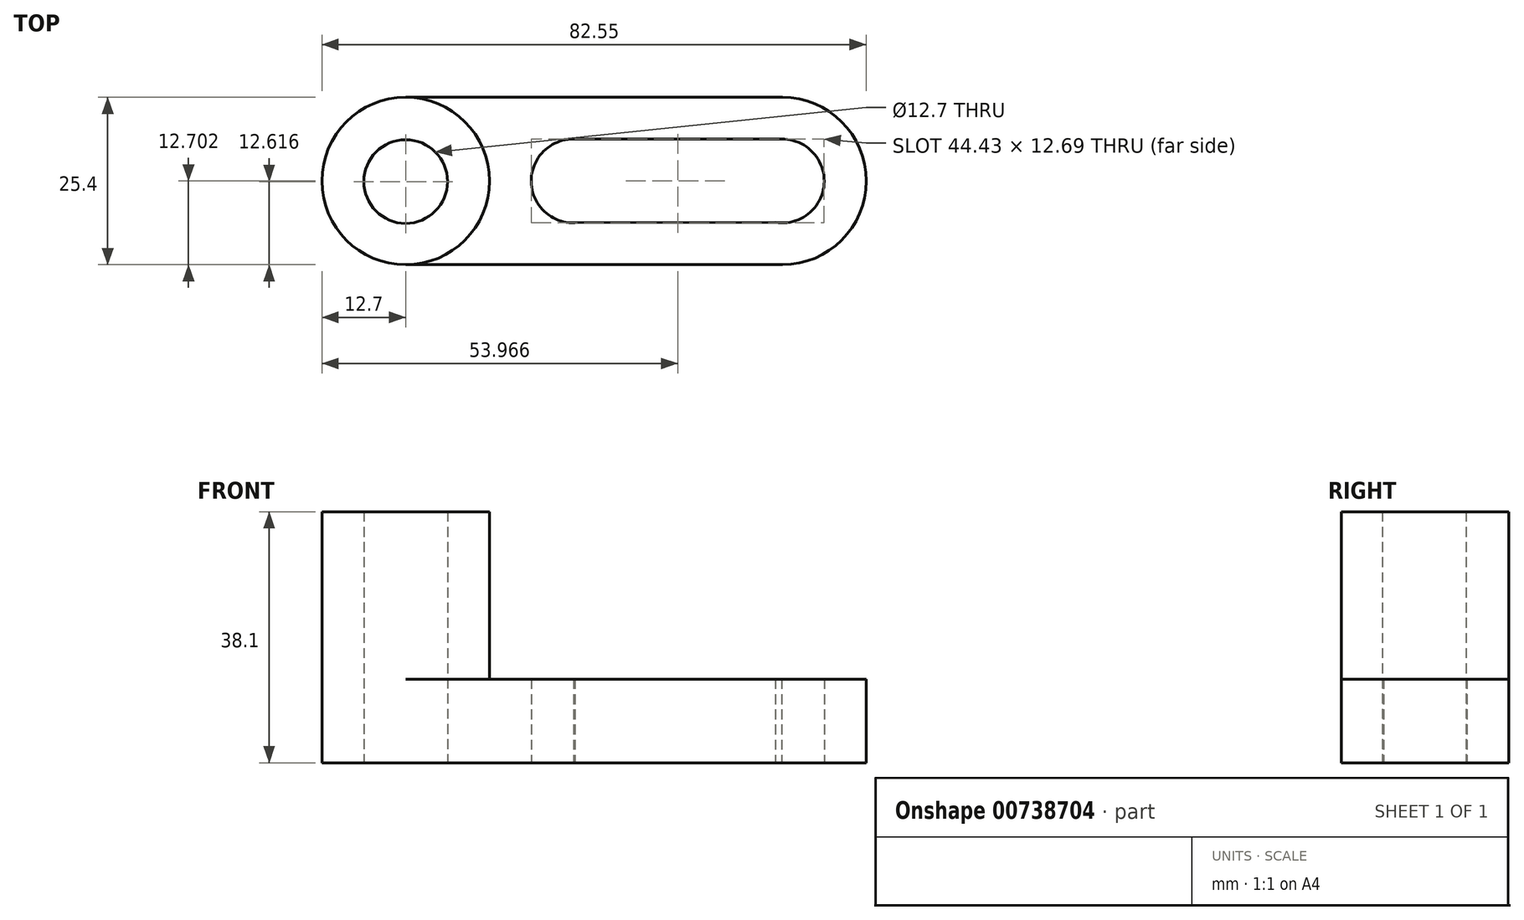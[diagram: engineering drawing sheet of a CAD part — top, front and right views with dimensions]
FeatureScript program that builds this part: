
annotation { "Feature Type Name" : "Feature", "Feature Type Description" : "" }
export const myFeature = defineFeature(function(context is Context, id is Id, definition is map)
    precondition{}
    {
        {
            var Q0;
            Q0=qCreatedBy(makeId("Front.planeOp"),FACE);
            var sketch = newSketch(context, id + "F0", { "sketchPlane" : qUnion([Q0])});
            skLineSegment(sketch, "E0", {"start": v(0, 38.1) * mm, "end": v(0, 0) * mm});
            skLineSegment(sketch, "E1", {"start": v(0, 0) * mm, "end": v(82.55, 0) * mm});
            skLineSegment(sketch, "E2", {"start": v(82.55, 0) * mm, "end": v(82.55, 12.7) * mm});
            skLineSegment(sketch, "E3", {"start": v(82.55, 12.7) * mm, "end": v(25.4, 12.7) * mm});
            skLineSegment(sketch, "E4", {"start": v(25.4, 12.7) * mm, "end": v(25.4, 38.1) * mm});
            skLineSegment(sketch, "E5", {"start": v(25.4, 38.1) * mm, "end": v(0, 38.1) * mm});
            skSolve(sketch);
        }
        {
            var Q0;
            Q0 = qSketchRegion(id + "F0", true);
            extrude(context, id + "F1", {"entities" : qUnion([Q0]), "depth" : 25.4 * mm, "offsetDistance" : 25.4 * mm});
        }
        {
            var Q0;
            Q0=qCreatedBy(makeId("Top.planeOp"),FACE);
            var sketch = newSketch(context, id + "F2", { "sketchPlane" : qUnion([Q0])});
            skCircle(sketch, "E6", {"center": v(12.7, -12.7) * mm, "radius": 12.7 * mm});
            skLineSegment(sketch, "E7", {"start": v(25.4, 0) * mm, "end": v(25.4, -25.4) * mm});
            skLineSegment(sketch, "E8", {"start": v(25.4, -25.4) * mm, "end": v(0, -25.4) * mm});
            skLineSegment(sketch, "E9", {"start": v(0, -25.4) * mm, "end": v(0, 0) * mm});
            skLineSegment(sketch, "E10", {"start": v(0, 0) * mm, "end": v(25.4, 0) * mm});
            skSolve(sketch);
        }
        {
            var Q0;
            Q0=qCreatedBy(makeId("Front.planeOp"),FACE);
            var sketch = newSketch(context, id + "F3", { "sketchPlane" : qUnion([Q0])});
            skLineSegment(sketch, "E11", {"start": v(25.4, 12.7) * mm, "end": v(0, 12.7) * mm});
            skLineSegment(sketch, "E12", {"start": v(0, 12.7) * mm, "end": v(0, 38.1) * mm});
            skLineSegment(sketch, "E13", {"start": v(0, 38.1) * mm, "end": v(25.4, 38.1) * mm});
            skLineSegment(sketch, "E14", {"start": v(25.4, 38.1) * mm, "end": v(25.4, 12.7) * mm});
            skSolve(sketch);
        }
        {
            var Q0;
            Q0 = qSketchRegion(id + "F3", true);
            extrude(context, id + "F4", {"entities" : qUnion([Q0]), "operationType" : NewBodyOperationType.REMOVE, "endBound" : BoundingType.THROUGH_ALL, "depth" : 25.4 * mm, "offsetDistance" : 25.4 * mm});
        }
        {
            var Q0;
            Q0=qCreatedBy(makeId("Top.planeOp"),FACE);
            var sketch = newSketch(context, id + "F5", { "sketchPlane" : qUnion([Q0])});
            skCircle(sketch, "E15", {"center": v(12.7, -12.7) * mm, "radius": 12.7 * mm});
            skSolve(sketch);
        }
        {
            var Q0;
            Q0 = qSketchRegion(id + "F5", true);
            extrude(context, id + "F6", {"entities" : qUnion([Q0]), "operationType" : NewBodyOperationType.ADD, "depth" : 38.1 * mm, "offsetDistance" : 25.4 * mm});
        }
        {
            var Q0;
            Q0=qCreatedBy(makeId("Top.planeOp"),FACE);
            var sketch = newSketch(context, id + "F7", { "sketchPlane" : qUnion([Q0])});
            skSolve(sketch);
        }
        {
            var Q0;
            Q0 = qSketchRegion(id + "F7", true);
            var Q1;
            {var subQ0=makeQuery(id+"F4.opExtrude","SWEPT_FACE",FACE,{"disambiguationData":[OSD([sQuery(id+"F3.wireOp",EDGE,"E11")])]});var subQ1=sQuery(id+"F0.wireOp",EDGE,"E3");var subQ2=sQuery(id+"F0.wireOp",EDGE,"E0");var subQ3=makeQuery(id+"F1.opExtrude","SWEPT_FACE",FACE,{"disambiguationData":[OSD([subQ1])]});Q1=makeQuery(id+"F6.boolean.opBoolean","SPLIT",FACE,{"disambiguationData":[TD([makeQuery(id+"F1.opExtrude","SWEPT_FACE",FACE,{"disambiguationData":[OSD([subQ2])]}),makeQuery(id+"F1.opExtrude","CAP_FACE",FACE,{"disambiguationData":[OSD([subQ2,sQuery(id+"F0.wireOp",EDGE,"E1"),sQuery(id+"F0.wireOp",EDGE,"E2"),subQ1,sQuery(id+"F0.wireOp",EDGE,"E4"),sQuery(id+"F0.wireOp",EDGE,"E5")])],"isStart":true}),subQ3,subQ0,makeQuery(id+"F6.opExtrude","SWEPT_FACE",FACE,{"disambiguationData":[OSD([sQuery(id+"F5.wireOp",EDGE,"E15")])]})])],"derivedFrom":makeQuery(id+"F4.boolean.opBoolean","MERGE",FACE,{"derivedFrom":[subQ3,subQ0]})});}
            var Q2;
            {var subQ0=makeQuery(id+"F4.opExtrude","SWEPT_FACE",FACE,{"disambiguationData":[OSD([sQuery(id+"F3.wireOp",EDGE,"E11")])]});var subQ1=sQuery(id+"F0.wireOp",EDGE,"E3");var subQ2=sQuery(id+"F0.wireOp",EDGE,"E0");var subQ3=makeQuery(id+"F1.opExtrude","SWEPT_FACE",FACE,{"disambiguationData":[OSD([subQ1])]});Q2=makeQuery(id+"F6.boolean.opBoolean","SPLIT",FACE,{"disambiguationData":[TD([makeQuery(id+"F1.opExtrude","SWEPT_FACE",FACE,{"disambiguationData":[OSD([subQ2])]}),makeQuery(id+"F1.opExtrude","CAP_FACE",FACE,{"disambiguationData":[OSD([subQ2,sQuery(id+"F0.wireOp",EDGE,"E1"),sQuery(id+"F0.wireOp",EDGE,"E2"),subQ1,sQuery(id+"F0.wireOp",EDGE,"E4"),sQuery(id+"F0.wireOp",EDGE,"E5")])],"isStart":false}),subQ3,subQ0,makeQuery(id+"F6.opExtrude","SWEPT_FACE",FACE,{"disambiguationData":[OSD([sQuery(id+"F5.wireOp",EDGE,"E15")])]})])],"derivedFrom":makeQuery(id+"F4.boolean.opBoolean","MERGE",FACE,{"derivedFrom":[subQ3,subQ0]})});}
            extrude(context, id + "F8", {"entities" : qUnion([Q0, Q1, Q2]), "operationType" : NewBodyOperationType.REMOVE, "endBound" : BoundingType.THROUGH_ALL, "oppositeDirection" : true, "depth" : 25.4 * mm, "offsetDistance" : 25.4 * mm});
        }
        {
            var Q0;
            Q0=qCreatedBy(makeId("Top.planeOp"),FACE);
            var sketch = newSketch(context, id + "F9", { "sketchPlane" : qUnion([Q0])});
            skCircle(sketch, "E16", {"center": v(69.85, -12.7) * mm, "radius": 6.35 * mm});
            skCircle(sketch, "E17", {"center": v(38.1, -12.7) * mm, "radius": 6.35 * mm});
            skLineSegment(sketch, "E18", {"start": v(38.01, -6.35) * mm, "end": v(69.94, -6.35) * mm});
            skLineSegment(sketch, "E19", {"start": v(37.89, -19.05) * mm, "end": v(70.93, -18.96) * mm});
            skSolve(sketch);
        }
        {
            var Q0;
            Q0 = qSketchRegion(id + "F9", true);
            extrude(context, id + "F10", {"entities" : qUnion([Q0]), "operationType" : NewBodyOperationType.REMOVE, "endBound" : BoundingType.THROUGH_ALL, "depth" : 25.4 * mm, "offsetDistance" : 25.4 * mm});
        }
        {
            var Q0;
            Q0=qCreatedBy(makeId("Top.planeOp"),FACE);
            var sketch = newSketch(context, id + "F11", { "sketchPlane" : qUnion([Q0])});
            skCircle(sketch, "E20", {"center": v(12.7, -12.78) * mm, "radius": 6.35 * mm});
            skSolve(sketch);
        }
        {
            var Q0;
            Q0 = qSketchRegion(id + "F11", true);
            extrude(context, id + "F12", {"entities" : qUnion([Q0]), "operationType" : NewBodyOperationType.REMOVE, "endBound" : BoundingType.THROUGH_ALL, "depth" : 25.4 * mm, "offsetDistance" : 25.4 * mm});
        }
        {
            var Q0;
            Q0=qCreatedBy(makeId("Top.planeOp"),FACE);
            var sketch = newSketch(context, id + "F13", { "sketchPlane" : qUnion([Q0])});
            skArc(sketch, "E21", {"start": v(69.85, -25.4) * mm, "mid": v(82.55, -12.7) * mm, "end": v(69.85, 0) * mm});
            skLineSegment(sketch, "E22", {"start": v(69.85, 0) * mm, "end": v(82.55, 0) * mm});
            skLineSegment(sketch, "E23", {"start": v(82.55, 0) * mm, "end": v(82.55, -25.4) * mm});
            skLineSegment(sketch, "E24", {"start": v(82.55, -25.4) * mm, "end": v(69.85, -25.4) * mm});
            skSolve(sketch);
        }
        {
            var Q0;
            Q0 = qSketchRegion(id + "F13", true);
            extrude(context, id + "F14", {"entities" : qUnion([Q0]), "operationType" : NewBodyOperationType.REMOVE, "endBound" : BoundingType.THROUGH_ALL, "depth" : 25.4 * mm, "offsetDistance" : 25.4 * mm});
        }
    });
